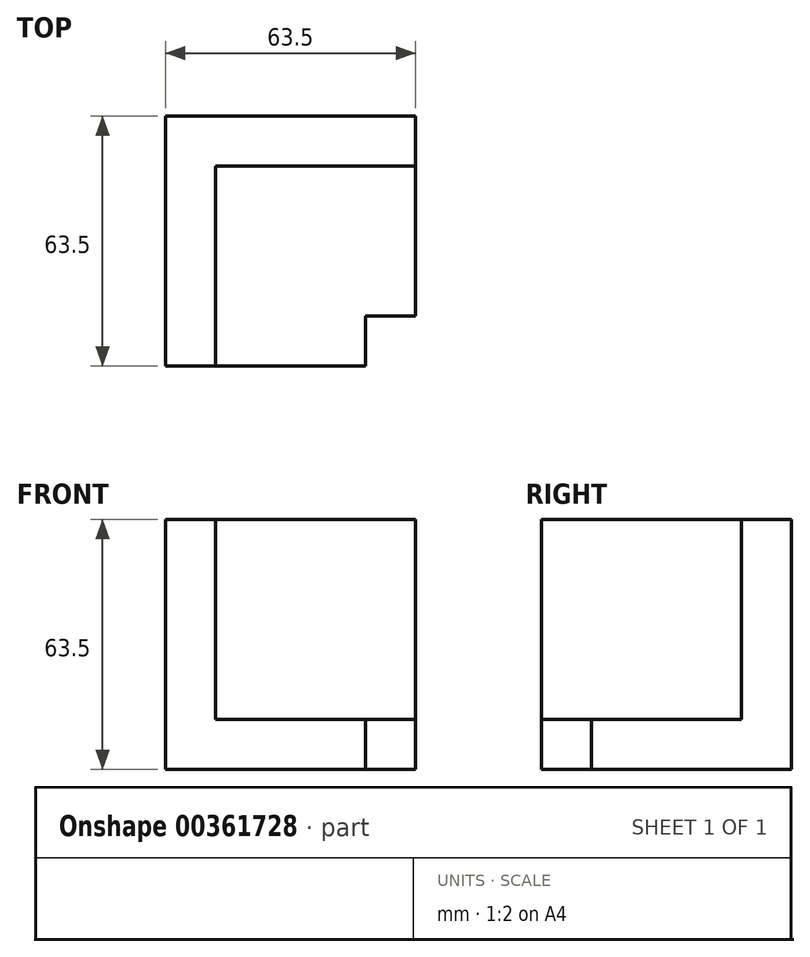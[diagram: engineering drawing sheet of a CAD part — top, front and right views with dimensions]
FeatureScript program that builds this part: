
annotation { "Feature Type Name" : "Feature", "Feature Type Description" : "" }
export const myFeature = defineFeature(function(context is Context, id is Id, definition is map)
    precondition{}
    {
        {
            var Q0;
            Q0=qCreatedBy(makeId("Front.planeOp"),FACE);
            var sketch = newSketch(context, id + "F0", { "sketchPlane" : qUnion([Q0])});
            skLineSegment(sketch, "E0.bottom", {"start": v(0, 0) * mm, "end": v(63.5, 0) * mm});
            skLineSegment(sketch, "E0.top", {"start": v(0, -63.5) * mm, "end": v(63.5, -63.5) * mm});
            skLineSegment(sketch, "E0.left", {"start": v(0, 0) * mm, "end": v(0, -63.5) * mm});
            skLineSegment(sketch, "E0.right", {"start": v(63.5, 0) * mm, "end": v(63.5, -63.5) * mm});
            skSolve(sketch);
        }
        {
            var Q0;
            Q0=makeQuery(id+"F0.imprint","IMPRINT",FACE,{"disambiguationData":[TD([[makeQuery(id+"F0.imprint","IMPRINT",EDGE,{"derivedFrom":sQuery(id+"F0.wireOp",EDGE,"E0.bottom")}),-1.0]])]});
            extrude(context, id + "F1", {"entities" : qUnion([Q0]), "depth" : 63.5 * mm});
        }
        {
            var Q0;
            Q0=makeQuery(id+"F1.opExtrude","CAP_FACE",FACE,{"disambiguationData":[OSD([sQuery(id+"F0.wireOp",EDGE,"E0.bottom"),sQuery(id+"F0.wireOp",EDGE,"E0.top"),sQuery(id+"F0.wireOp",EDGE,"E0.left"),sQuery(id+"F0.wireOp",EDGE,"E0.right")])],"isStart":false});
            var sketch = newSketch(context, id + "F2", { "sketchPlane" : qUnion([Q0])});
            skLineSegment(sketch, "E1.bottom", {"start": v(12.7, 0) * mm, "end": v(63.5, 0) * mm});
            skLineSegment(sketch, "E1.top", {"start": v(12.7, -50.8) * mm, "end": v(63.5, -50.8) * mm});
            skLineSegment(sketch, "E1.left", {"start": v(12.7, 0) * mm, "end": v(12.7, -50.8) * mm});
            skLineSegment(sketch, "E1.right", {"start": v(63.5, 0) * mm, "end": v(63.5, -50.8) * mm});
            skSolve(sketch);
        }
        {
            var Q0;
            Q0=makeQuery(id+"F2.imprint","IMPRINT",FACE,{"disambiguationData":[TD([[makeQuery(id+"F2.imprint","IMPRINT",EDGE,{"derivedFrom":sQuery(id+"F2.wireOp",EDGE,"E1.bottom")}),-1.0]])]});
            extrude(context, id + "F3", {"entities" : qUnion([Q0]), "operationType" : NewBodyOperationType.REMOVE, "oppositeDirection" : true, "depth" : 50.8 * mm});
        }
        {
            var Q0;
            Q0=makeQuery(id+"F3.boolean.opBoolean","COPY",FACE,{"derivedFrom":makeQuery(id+"F3.opExtrude","SWEPT_FACE",FACE,{"disambiguationData":[OSD([sQuery(id+"F2.wireOp",EDGE,"E1.top")])]})});
            var sketch = newSketch(context, id + "F4", { "sketchPlane" : qUnion([Q0])});
            skLineSegment(sketch, "E2.bottom", {"start": v(50.8, -50.8) * mm, "end": v(63.5, -50.8) * mm});
            skLineSegment(sketch, "E2.top", {"start": v(50.8, -63.5) * mm, "end": v(63.5, -63.5) * mm});
            skLineSegment(sketch, "E2.left", {"start": v(50.8, -50.8) * mm, "end": v(50.8, -63.5) * mm});
            skLineSegment(sketch, "E2.right", {"start": v(63.5, -50.8) * mm, "end": v(63.5, -63.5) * mm});
            skSolve(sketch);
        }
        {
            var Q0;
            Q0=makeQuery(id+"F4.imprint","IMPRINT",FACE,{"disambiguationData":[TD([[makeQuery(id+"F4.imprint","IMPRINT",EDGE,{"derivedFrom":sQuery(id+"F4.wireOp",EDGE,"E2.bottom")}),-1.0]])]});
            extrude(context, id + "F5", {"entities" : qUnion([Q0]), "operationType" : NewBodyOperationType.REMOVE, "oppositeDirection" : true, "depth" : 12.7 * mm});
        }
    });
